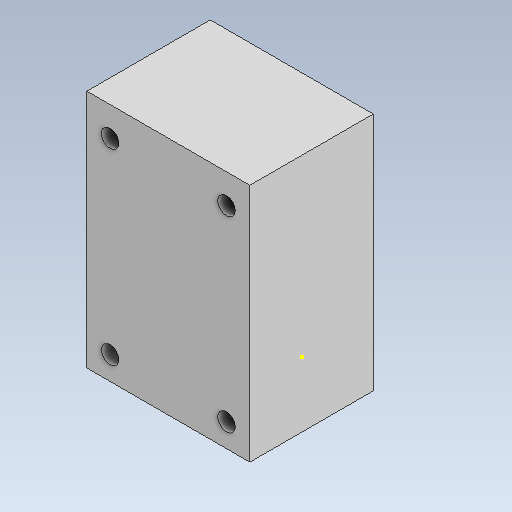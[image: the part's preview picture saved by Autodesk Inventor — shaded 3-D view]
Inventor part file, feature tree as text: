
AUTODESK INVENTOR PART (.ipt)
format: ipt  version: 2020 (Build 240168000, 168)  size: 145,408 bytes
history: native  units: in
note: dims shown in document units (in); Inventor stores cm internally (conversion verified against a paired STEP export)
features: reference x7, sketch x4, other x4, extrude x3
ambient origin geometry x8: Origin, YZ Plane, XZ Plane, XY Plane, X Axis, Y Axis, Z Axis, Center Point
bodies: Solid1 (feature_tree)
feature tree (18):
  extrude  "Extrusion1"  Depth=1.125in
  extrude  "Extrusion2"  Depth=0.25in TaperAngle=0.0deg
  extrude  "Extrusion3"  Depth=0.25in
  sketch  "Sketch4"  dims[d8=0.25in d9=0.75in d10=0.0in]
  sketch  "Sketch1"  dims[d0=0.625in d1=1.125in]
  reference  "Reference1"
  reference  "Reference2"
  reference  "Reference3"
  reference  "Reference4"
  sketch  "Sketch2"  dims[d2=1.325in d3=0.0in d4=0.25in d5=0.0in]
  sketch  "Sketch3"  dims[d6=0.1875in d7=0.25in]
  reference  "Reference5"
  reference  "Reference6"
  reference  "Reference7"
  other  "<userpath>\Desktop\PnP Machine\PnP Machine.iam"
  other  "PnP Machine.iam"
  other  "YClamp:1"
  other  "6497K113_HIGH-STRENGTH HTD TIMING BELT PULLEY:7"
